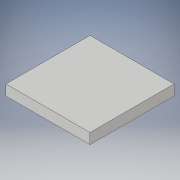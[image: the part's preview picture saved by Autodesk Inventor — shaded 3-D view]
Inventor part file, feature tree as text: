
AUTODESK INVENTOR PART (.ipt)
format: ipt  version: 2017 (Build 210142000, 142)  size: 87,552 bytes
history: native  units: in
note: dims shown in document units (in); Inventor stores cm internally (conversion verified against a paired STEP export)
features: extrude x1, sketch x1
ambient origin geometry x8: Origin, YZ Plane, XZ Plane, XY Plane, X Axis, Y Axis, Z Axis, Center Point
bodies: Solid1 (feature_tree)
feature tree (2):
  extrude  "Extrusion1"  Depth=6.0in
  sketch  "Sketch1"  dims[d0=6.0in d1=6.0in d2=0.75in d3=0.0in]
